# Revit family: 304_feb3d3af865c4812a1f7d694539fd2
name_source: partatom
category: Pipe Accessories
units: mm (PartAtom-declared; Revit-internal decimal feet)

## family parameters
Always vertical = Yes
Cut with Voids When Loaded = No
Part Type = Valve - Breaks Into
Round Connector Dimension = Use Diameter
Shared = No
Work Plane-Based = No

## types (4) — shared parameters
A = 45.00°
CAT0 = Yes
Description = PI zone valve, Internal thread with measuring nipple
H1 = 10 mm  [stored 0.0328084 ft]
H1__ve = -10 mm  [stored -0.0328084 ft]
H2 = 4 mm  [stored 0.0131234 ft]
H2__ve = -4 mm  [stored -0.0131234 ft]
H3 = 3 mm  [stored 0.00984252 ft]
L2 = 12 mm  [stored 0.0393701 ft]
L2D = 96 mm  [stored 0.314961 ft]
L2D_Min = 3048 mm  [stored 10 ft]
Manufacturer = Belimo
QmdConnectorList = 301;D;302;D
R2 = 6 mm  [stored 0.019685 ft]
R3 = 4 mm  [stored 0.0131234 ft]
R4 = 9 mm  [stored 0.0295276 ft]
S1 = 6 mm  [stored 0.019685 ft]
S2 = 4 mm  [stored 0.0131234 ft]
W2D = 15 mm  [stored 0.0492126 ft]
magiPartTypeId = 304
magiProductFamilyId = feb3d3af865c4812a1f7d694539fd2

## per-type parameters (varying)
| type | CenSd_R_6 | D | H | L1 | L1__ve | L3 | L4 | LL | LM | LM2 | NL | R | R1 | Y | Z | magiProductId |
| C215QPT-B | 13 mm | 15 mm | 26 mm  [stored 0.0853018 ft] | 14 mm  [stored 0.0459318 ft] | -14 mm  [stored -0.0459318 ft] | 44 mm  [stored 0.144357 ft] | 34 mm  [stored 0.111549 ft] | 48 mm  [stored 0.15748 ft] | 36 mm  [stored 0.11811 ft] | 24 mm  [stored 0.0787402 ft] | 60 mm  [stored 0.19685 ft] | 15 mm  [stored 0.0492126 ft] | 26 mm  [stored 0.0853018 ft] | 12 mm  [stored 0.0393701 ft] | 5 mm  [stored 0.0164042 ft] | 1e97b40b745d42c994ccf3891833be |
| C215QPT-D | 13 mm | 15 mm | 26 mm  [stored 0.0853018 ft] | 14 mm  [stored 0.0459318 ft] | -14 mm  [stored -0.0459318 ft] | 44 mm  [stored 0.144357 ft] | 34 mm  [stored 0.111549 ft] | 48 mm  [stored 0.15748 ft] | 36 mm  [stored 0.11811 ft] | 24 mm  [stored 0.0787402 ft] | 60 mm  [stored 0.19685 ft] | 15 mm  [stored 0.0492126 ft] | 26 mm  [stored 0.0853018 ft] | 12 mm  [stored 0.0393701 ft] | 5 mm  [stored 0.0164042 ft] | 620c07cdd3c042c1a765e833e414cb |
| C220QPT-F | 15 mm  [stored 0.0492126 ft] | 20 mm | 31 mm  [stored 0.101706 ft] | 14 mm  [stored 0.0459318 ft] | -14 mm  [stored -0.0459318 ft] | 54 mm  [stored 0.177165 ft] | 39 mm  [stored 0.127953 ft] | 53 mm  [stored 0.173885 ft] | 42 mm  [stored 0.137795 ft] | 22 mm  [stored 0.0721785 ft] | 65 mm  [stored 0.213255 ft] | 17 mm  [stored 0.0557743 ft] | 32 mm | 16 mm  [stored 0.0524934 ft] | 12 mm  [stored 0.0393701 ft] | c1f24b3ba6694597a87517c4ea3bf7 |
| C225QPT-G | 17 mm  [stored 0.0557743 ft] | 25 mm | 40 mm  [stored 0.131234 ft] | 18 mm  [stored 0.0590551 ft] | -18 mm  [stored -0.0590551 ft] | 58 mm  [stored 0.190289 ft] | 42 mm  [stored 0.137795 ft] | 59 mm  [stored 0.19357 ft] | 45 mm  [stored 0.147638 ft] | 28 mm  [stored 0.0918635 ft] | 60 mm  [stored 0.19685 ft] | 20 mm  [stored 0.0656168 ft] | 39 mm  [stored 0.127953 ft] | 18 mm  [stored 0.0590551 ft] | 26 mm  [stored 0.0853018 ft] | a7725baab0894ae99b7cbc0d0a09a4 |

note: column(s) folded — value = type name in every type: MC Product Code

note: [stored X ft] marks values corroborated as IEEE doubles in the binary element streams (Revit-internal decimal feet)

## geometry (parser evidence)
native form markers: Blend x2, Sweep x3
no freeform markers — native parametric forms only
